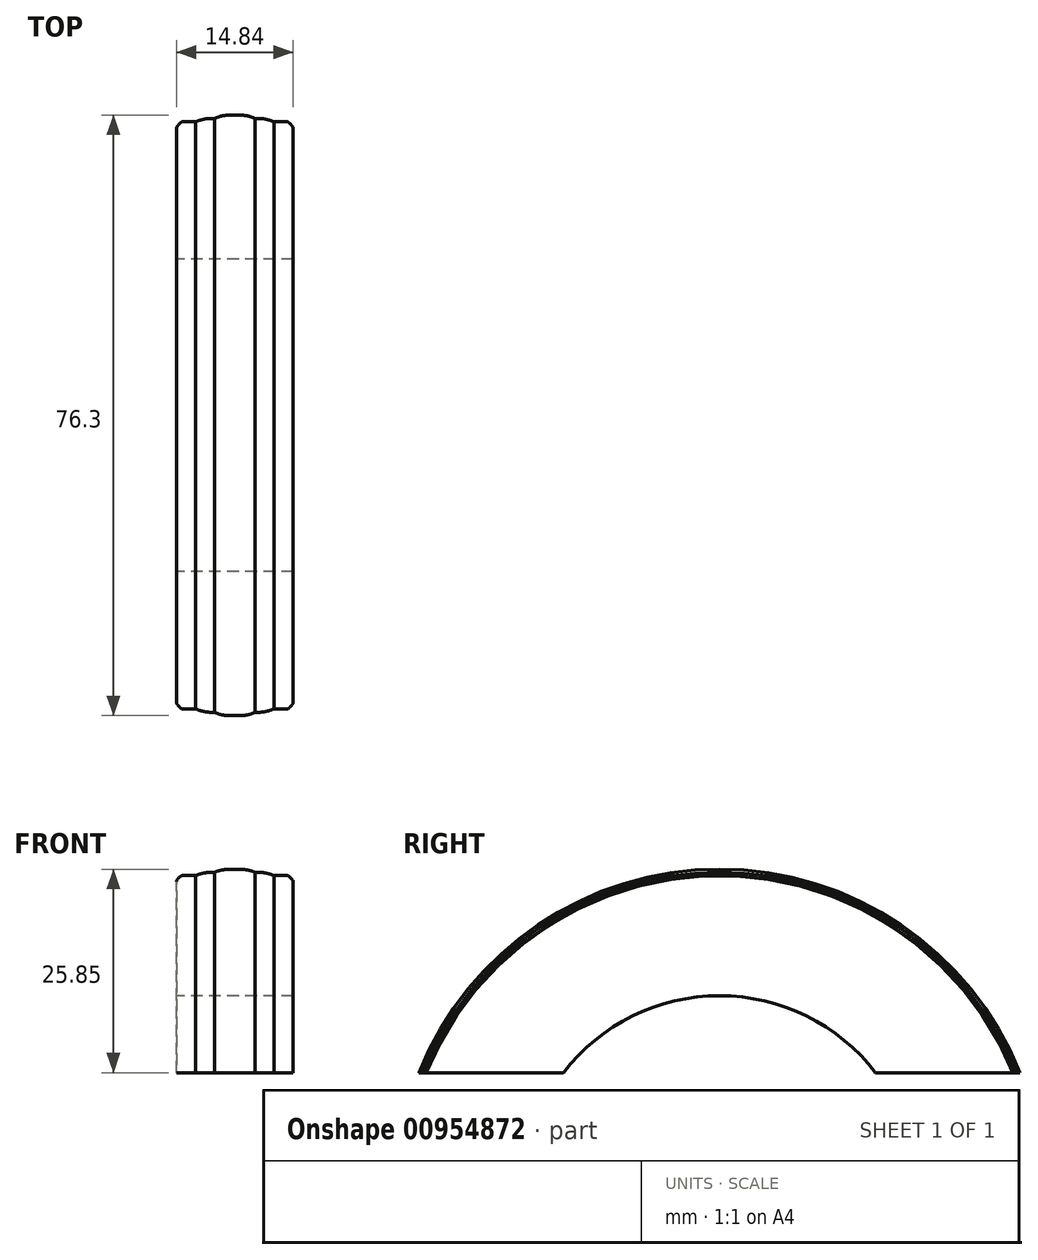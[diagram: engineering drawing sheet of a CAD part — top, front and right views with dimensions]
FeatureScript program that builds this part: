
annotation { "Feature Type Name" : "Feature", "Feature Type Description" : "" }
export const myFeature = defineFeature(function(context is Context, id is Id, definition is map)
    precondition{}
    {
        {
            var Q0;
            Q0=qCreatedBy(makeId("Front.planeOp"),FACE);
            var sketch = newSketch(context, id + "F0", { "sketchPlane" : qUnion([Q0])});
            skLineSegment(sketch, "E0", {"start": v(-55.67, 0) * mm, "end": v(68.03, 0) * mm, "construction": true});
            skLineSegment(sketch, "E1", {"start": v(-7.42, 0) * mm, "end": v(-7.42, 40.28) * mm});
            skLineSegment(sketch, "E2", {"start": v(-7.42, 40.28) * mm, "end": v(-4.96, 40.28) * mm});
            skLineSegment(sketch, "E3", {"start": v(-4.96, 40.28) * mm, "end": v(-4.96, 40.68) * mm});
            skLineSegment(sketch, "E4", {"start": v(-4.96, 40.68) * mm, "end": v(-2.58, 40.68) * mm});
            skLineSegment(sketch, "E5", {"start": v(-2.58, 40.68) * mm, "end": v(-2.58, 41.08) * mm});
            skLineSegment(sketch, "E6", {"start": v(-2.58, 41.08) * mm, "end": v(2.58, 41.08) * mm});
            skLineSegment(sketch, "E7", {"start": v(2.58, 41.08) * mm, "end": v(2.58, 40.68) * mm});
            skLineSegment(sketch, "E8", {"start": v(2.58, 40.68) * mm, "end": v(4.96, 40.68) * mm});
            skLineSegment(sketch, "E9", {"start": v(4.96, 40.68) * mm, "end": v(4.96, 40.28) * mm});
            skLineSegment(sketch, "E10", {"start": v(4.96, 40.28) * mm, "end": v(7.42, 40.28) * mm});
            skLineSegment(sketch, "E11", {"start": v(7.42, 40.28) * mm, "end": v(7.42, 0) * mm});
            skLineSegment(sketch, "E12", {"start": v(7.42, 0) * mm, "end": v(-7.42, 0) * mm});
            skLineSegment(sketch, "E13", {"start": v(0, 0) * mm, "end": v(0, 47.43) * mm, "construction": true});
            skSolve(sketch);
        }
        {
            var Q0;
            Q0=makeQuery(id+"F0.imprint","IMPRINT",FACE,{"disambiguationData":[TD([[makeQuery(id+"F0.imprint","IMPRINT",EDGE,{"derivedFrom":sQuery(id+"F0.wireOp",EDGE,"E1")}),-1.0]])]});
            var Q1;
            Q1=sQuery(id+"F0.wireOp",EDGE,"E0");
            revolve(context, id + "F1", {"surfaceOperationType" : NewSurfaceOperationType.NEW, "entities" : qUnion([Q0]), "axis" : qUnion([Q1]), "revolveType" : RevolveType.FULL});
        }
        {
            var Q0;
            Q0=makeQuery(id+"F1.opRevolve","SWEPT_EDGE",EDGE,{"disambiguationData":[OSD([sQuery(id+"F0.wireOp",EDGE,"E10"),sQuery(id+"F0.wireOp",EDGE,"E11")])]});
            var Q1;
            Q1=makeQuery(id+"F1.opRevolve","SWEPT_EDGE",EDGE,{"disambiguationData":[OSD([sQuery(id+"F0.wireOp",EDGE,"E1"),sQuery(id+"F0.wireOp",EDGE,"E2")])]});
            fillet(context, id + "F2", {"entities" : qUnion([Q0, Q1]), "radius" : 0.76 * mm, "tangentPropagation" : true, "rho" : 0.2, "crossSection" : FilletCrossSection.CONIC, "allowEdgeOverflow" : false});
        }
        {
            var Q0;
            Q0=makeQuery(id+"F1.opRevolve","SWEPT_EDGE",EDGE,{"disambiguationData":[OSD([sQuery(id+"F0.wireOp",EDGE,"E8"),sQuery(id+"F0.wireOp",EDGE,"E9")])]});
            var Q1;
            Q1=makeQuery(id+"F1.opRevolve","SWEPT_EDGE",EDGE,{"disambiguationData":[OSD([sQuery(id+"F0.wireOp",EDGE,"E3"),sQuery(id+"F0.wireOp",EDGE,"E4")])]});
            fillet(context, id + "F3", {"entities" : qUnion([Q0, Q1]), "radius" : 5.08 * mm, "tangentPropagation" : true, "allowEdgeOverflow" : false});
        }
        {
            var Q0;
            Q0=makeQuery(id+"F1.opRevolve","SWEPT_EDGE",EDGE,{"disambiguationData":[OSD([sQuery(id+"F0.wireOp",EDGE,"E6"),sQuery(id+"F0.wireOp",EDGE,"E7")])]});
            var Q1;
            Q1=makeQuery(id+"F1.opRevolve","SWEPT_EDGE",EDGE,{"disambiguationData":[OSD([sQuery(id+"F0.wireOp",EDGE,"E5"),sQuery(id+"F0.wireOp",EDGE,"E6")])]});
            fillet(context, id + "F4", {"entities" : qUnion([Q0, Q1]), "radius" : 5.08 * mm, "tangentPropagation" : true, "allowEdgeOverflow" : false});
        }
        {
            var Q0;
            Q0=qCreatedBy(makeId("Right.planeOp"),FACE);
            var sketch = newSketch(context, id + "F5", { "sketchPlane" : qUnion([Q0])});
            skCircle(sketch, "E14", {"center": v(0, 0) * mm, "radius": 25 * mm});
            skSolve(sketch);
        }
        {
            var Q0;
            Q0=qSketchRegion(id+"F5",true);
            extrude(context, id + "F6", {"entities" : qUnion([Q0]), "operationType" : NewBodyOperationType.REMOVE, "endBound" : BoundingType.THROUGH_ALL, "depth" : 25.4 * mm, "offsetDistance" : 25.4 * mm, "hasSecondDirection" : true, "secondDirectionBound" : SecondDirectionBoundingType.THROUGH_ALL, "secondDirectionOppositeDirection" : true, "secondDirectionDepth" : 25.4 * mm});
        }
        {
            var Q0;
            Q0=qCreatedBy(makeId("Right.planeOp"),FACE);
            var sketch = newSketch(context, id + "F7", { "sketchPlane" : qUnion([Q0])});
            skLineSegment(sketch, "E15", {"start": v(0, 15.23) * mm, "end": v(-38.1, 15.23) * mm, "construction": true});
            skLineSegment(sketch, "E16.MirrorCS", {"start": v(0, 15.23) * mm, "end": v(38.1, 15.23) * mm, "construction": true});
            skLineSegment(sketch, "E17", {"start": v(-59.25, 15.23) * mm, "end": v(65.7, 15.23) * mm});
            skLineSegment(sketch, "E18", {"start": v(65.7, 15.23) * mm, "end": v(65.7, -43.9) * mm});
            skLineSegment(sketch, "E19", {"start": v(65.7, -43.9) * mm, "end": v(-59.25, -43.9) * mm});
            skLineSegment(sketch, "E20", {"start": v(-59.25, -43.9) * mm, "end": v(-59.25, 15.23) * mm});
            skSolve(sketch);
        }
        {
            var Q0;
            Q0 = qSketchRegion(id + "F7", true);
            extrude(context, id + "F8", {"entities" : qUnion([Q0]), "operationType" : NewBodyOperationType.REMOVE, "endBound" : BoundingType.THROUGH_ALL, "oppositeDirection" : true, "depth" : 25.4 * mm, "offsetDistance" : 25.4 * mm, "hasSecondDirection" : true, "secondDirectionBound" : SecondDirectionBoundingType.THROUGH_ALL, "secondDirectionOppositeDirection" : false, "secondDirectionDepth" : 25.4 * mm});
        }
    });
